# Revit family: NLRS_27_GM_LIB_GNI_MR
name_source: partatom
category: Generic Models
revit_build: Autodesk Revit 2017 (Build: 20190507_1515(x64)
units: mm (PartAtom-declared; Revit-internal decimal feet)

## family parameters
Can host rebar = No
Cut with Voids When Loaded = Yes
Part Type = Normal
Room Calculation Point = No
Round Connector Dimension = Use Diameter
Shared = No

## types (2) — shared parameters
03_druppel = Yes
Assembly Code = 27.16
Description = GNI Goot
Diepte_bak = 88 mm  [stored 0.288714 ft]
IfcExportAs = IfcFlowsegment
Manufacturer = Meilof Riks bv
Model = GNI
NLRS_C_Materiaal = RAL 9010
Set_Diepte_bak = 88 mm  [stored 0.288714 ft]
Type Image = <None>
URL = https://www.meilofriks.nl
Vorm_Goot_L = 01 : 2_←_Hoek_L
Vorm_Goot_L-R = 01 : 4_↔_Hoek_L-R
Vorm_Goot_R = 01 : 3_→_Hoek_R

## per-type parameters (varying)
| type | Breedte_goot | Breedte_goot_hoek | Hoogte_AK | Hoogte_VK | NLRS_C_Binnenbak | set_Hoogte_AK |
| GNI235 | 235 mm | 235 mm | 215 mm | 169 mm | RAL 9010 | 215 mm |
| GNI310 | 310 mm  [stored 1.01706 ft] | 310 mm  [stored 1.01706 ft] | 240 mm  [stored 0.787402 ft] | 185 mm  [stored 0.606955 ft] | RAL 7036 | 240 mm  [stored 0.787402 ft] |

note: [stored X ft] marks values corroborated as IEEE doubles in the binary element streams (Revit-internal decimal feet)

## geometry (parser evidence)
native form markers: Sweep x28
no freeform markers — native parametric forms only
